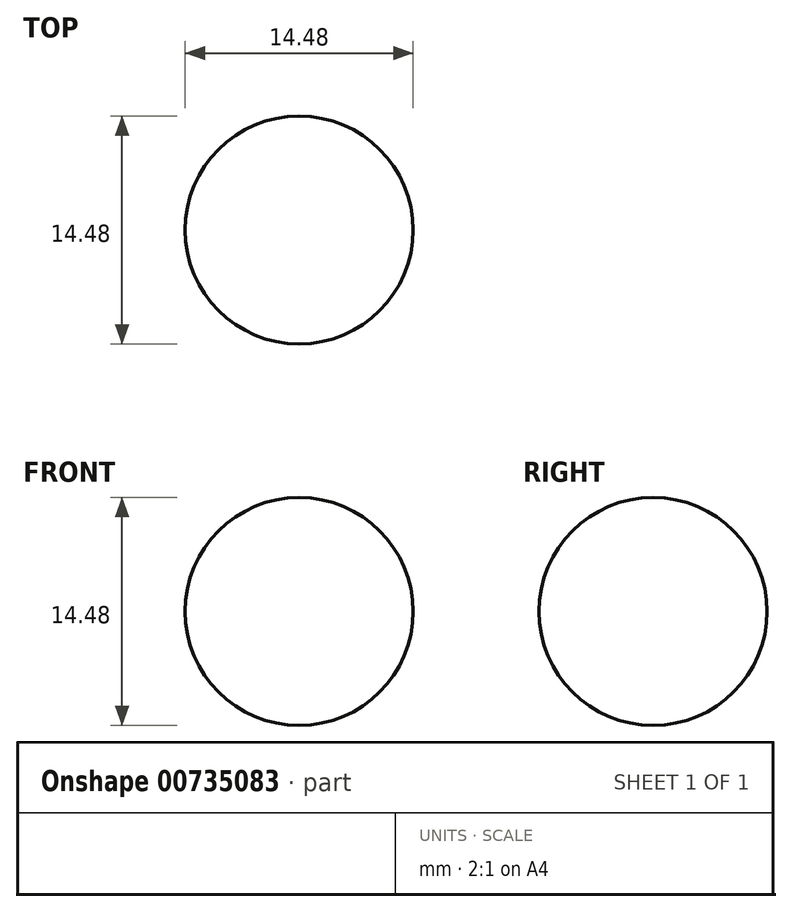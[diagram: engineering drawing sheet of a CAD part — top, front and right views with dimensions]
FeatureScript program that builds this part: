
annotation { "Feature Type Name" : "Feature", "Feature Type Description" : "" }
export const myFeature = defineFeature(function(context is Context, id is Id, definition is map)
    precondition{}
    {
        {
            var Q0;
            Q0=qCreatedBy(makeId("Top.planeOp"),FACE);
            var sketch = newSketch(context, id + "F0", { "sketchPlane" : qUnion([Q0])});
            skLineSegment(sketch, "E0", {"start": v(0, -7.24) * mm, "end": v(0, 7.24) * mm});
            skLineSegment(sketch, "E1", {"start": v(0, 7.24) * mm, "end": v(0, 7.24) * mm});
            skArc(sketch, "E2", {"start": v(0, -7.24) * mm, "mid": v(7.24, 0) * mm, "end": v(0, 7.24) * mm});
            skLineSegment(sketch, "E3", {"start": v(0, 0) * mm, "end": v(3.63, 0) * mm});
            skPoint(sketch, "E3.endSnap0", {"position": v(7.24, 0) * mm});
            skLineSegment(sketch, "E4", {"start": v(3.63, 0) * mm, "end": v(3.63, 6.26) * mm});
            skSolve(sketch);
        }
        {
            var Q0;
            Q0=sQuery(id+"F0.wireOp",EDGE,"E2");
            var Q1;
            Q1=sQuery(id+"F0.wireOp",EDGE,"E0");
            revolve(context, id + "F1", {"bodyType" : ToolBodyType.SURFACE, "surfaceOperationType" : NewSurfaceOperationType.NEW, "surfaceEntities" : qUnion([Q0]), "axis" : qUnion([Q1]), "revolveType" : RevolveType.FULL});
        }
    });
